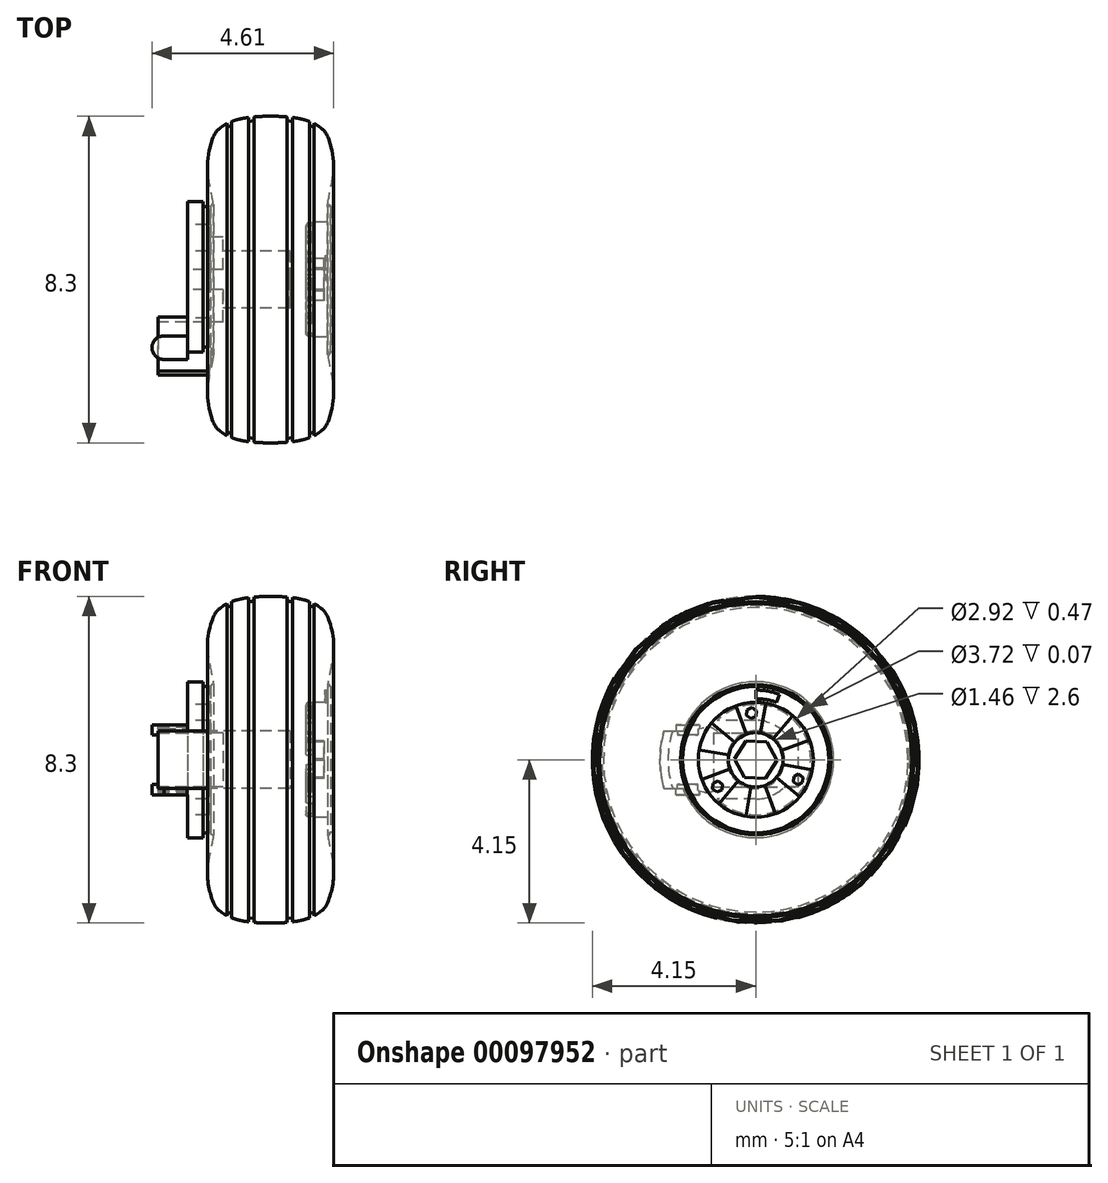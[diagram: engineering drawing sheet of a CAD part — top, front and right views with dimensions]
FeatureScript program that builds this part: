
annotation { "Feature Type Name" : "Feature", "Feature Type Description" : "" }
export const myFeature = defineFeature(function(context is Context, id is Id, definition is map)
    precondition{}
    {
        {
            var Q0;
            Q0=qCreatedBy(makeId("Front.planeOp"),FACE);
            var sketch = newSketch(context, id + "F0", { "sketchPlane" : qUnion([Q0])});
            skLineSegment(sketch, "E0.bottom", {"start": v(0, 0) * mm, "end": v(1.1, 0) * mm});
            skLineSegment(sketch, "E0.top", {"start": v(0.98, 0.7) * mm, "end": v(1.1, 0.7) * mm});
            skLineSegment(sketch, "E0.right", {"start": v(1.11, 0) * mm, "end": v(1.11, 0.7) * mm});
            skLineSegment(sketch, "E1", {"start": v(0.9, 0.77) * mm, "end": v(0.9, 1.38) * mm});
            skLineSegment(sketch, "E2", {"start": v(0.98, 1.46) * mm, "end": v(1.27, 1.46) * mm});
            skLineSegment(sketch, "E3", {"start": v(1.45, 1.64) * mm, "end": v(1.45, 1.86) * mm});
            skLineSegment(sketch, "E4", {"start": v(1.45, 1.91) * mm, "end": v(1.45, 1.91) * mm});
            skLineSegment(sketch, "E5", {"start": v(1.52, 1.91) * mm, "end": v(1.52, 1.91) * mm});
            skLineSegment(sketch, "E6", {"start": v(1.47, 1.91) * mm, "end": v(1.45, 1.91) * mm});
            skPoint(sketch, "E7.orphan", {"position": v(0, 1.46) * mm});
            skPoint(sketch, "E8.visualSharp", {"position": v(1.45, 1.46) * mm});
            skPoint(sketch, "E9.visualSharp", {"position": v(0.9, 1.46) * mm});
            skArc(sketch, "E9.filletArc", {"start": v(0.98, 1.46) * mm, "mid": v(0.92, 1.44) * mm, "end": v(0.9, 1.38) * mm});
            skArc(sketch, "E10.filletArc", {"start": v(0.9, 0.77) * mm, "mid": v(0.92, 0.71) * mm, "end": v(0.98, 0.7) * mm});
            skPoint(sketch, "E11.visualSharp", {"position": v(1.52, 1.91) * mm});
            skArc(sketch, "E11.filletArc", {"start": v(1.52, 1.86) * mm, "mid": v(1.5, 1.9) * mm, "end": v(1.47, 1.91) * mm});
            skLineSegment(sketch, "E12", {"start": v(-0.76, 4.15) * mm, "end": v(0, 4.15) * mm, "construction": true});
            skLineSegment(sketch, "E13", {"start": v(1.6, 4.08) * mm, "end": v(1.6, 0.98) * mm, "construction": true});
            skFitSpline(sketch, "E14", {"points": [v(0, 4.15) * mm, v(1.28, 3.85) * mm, v(1.4, 3.73) * mm, v(1.6, 2.99) * mm, v(1.45, 1.91) * mm], "startDerivative": vector(8.32, 0) * mm, "endDerivative": vector(-0.59, -3.7) * mm});
            skLineSegment(sketch, "E15", {"start": v(0, 4.15) * mm, "end": v(1.72, 4.15) * mm, "construction": true});
            skLineSegment(sketch, "E16", {"start": v(0.42, 4.03) * mm, "end": v(0.56, 4.02) * mm});
            skLineSegment(sketch, "E17", {"start": v(0.99, 3.92) * mm, "end": v(1.1, 3.87) * mm});
            skLineSegment(sketch, "E18", {"start": v(0.42, 4.03) * mm, "end": v(0.42, 4.13) * mm});
            skLineSegment(sketch, "E19", {"start": v(0.56, 4.02) * mm, "end": v(0.56, 4.12) * mm});
            skLineSegment(sketch, "E20", {"start": v(0.99, 3.92) * mm, "end": v(0.99, 4.02) * mm});
            skLineSegment(sketch, "E21", {"start": v(1.1, 3.87) * mm, "end": v(1.1, 3.97) * mm});
            skLineSegment(sketch, "E22", {"start": v(1.52, 1.86) * mm, "end": v(1.45, 1.86) * mm});
            skLineSegment(sketch, "E23", {"start": v(1.27, 1.46) * mm, "end": v(1.45, 1.46) * mm});
            skLineSegment(sketch, "E24", {"start": v(1.45, 1.46) * mm, "end": v(1.45, 1.64) * mm});
            skLineSegment(sketch, "E25.MirrorCS", {"start": v(-1.11, 0) * mm, "end": v(-1.11, 0.7) * mm, "construction": true});
            skLineSegment(sketch, "E26.MirrorCS", {"start": v(-0.98, 0.7) * mm, "end": v(-1.1, 0.7) * mm, "construction": true});
            skArc(sketch, "E27.MirrorCS", {"start": v(-0.9, 0.77) * mm, "mid": v(-0.92, 0.71) * mm, "end": v(-0.98, 0.7) * mm, "construction": true});
            skLineSegment(sketch, "E28.MirrorCS", {"start": v(-0.9, 0.77) * mm, "end": v(-0.9, 1.38) * mm, "construction": true});
            skArc(sketch, "E29.MirrorCS", {"start": v(-1.52, 1.86) * mm, "mid": v(-1.5, 1.9) * mm, "end": v(-1.47, 1.91) * mm});
            skLineSegment(sketch, "E30.MirrorCS", {"start": v(-1.47, 1.91) * mm, "end": v(-1.45, 1.91) * mm});
            skLineSegment(sketch, "E31", {"start": v(-2.1, 1.98) * mm, "end": v(-2.1, 1.4) * mm});
            skLineSegment(sketch, "E32", {"start": v(-2.1, 1.98) * mm, "end": v(-1.71, 1.98) * mm});
            skLineSegment(sketch, "E33", {"start": v(-2.1, 1.4) * mm, "end": v(-1.61, 1.4) * mm});
            skPoint(sketch, "E34.orphan", {"position": v(-2.1, 0.82) * mm});
            skLineSegment(sketch, "E35", {"start": v(-1.61, 0.73) * mm, "end": v(0.49, 0.73) * mm});
            skLineSegment(sketch, "E36", {"start": v(0.49, 0) * mm, "end": v(0.49, 0.96) * mm});
            skLineSegment(sketch, "E37", {"start": v(-0.97, 1.4) * mm, "end": v(-0.97, 0.96) * mm, "construction": true});
            skLineSegment(sketch, "E38", {"start": v(-1.71, 1.98) * mm, "end": v(-1.71, 1.86) * mm});
            skLineSegment(sketch, "E39", {"start": v(-1.52, 1.86) * mm, "end": v(-1.71, 1.86) * mm});
            skLineSegment(sketch, "E40", {"start": v(-2.64, 1.27) * mm, "end": v(-2.64, -0.73) * mm, "construction": true});
            skLineSegment(sketch, "E41", {"start": v(-1.61, 1.4) * mm, "end": v(-1.61, 0.73) * mm});
            skPoint(sketch, "E42.orphan", {"position": v(0, 0.73) * mm});
            skLineSegment(sketch, "E43", {"start": v(-1.61, 1.4) * mm, "end": v(-0.97, 1.4) * mm, "construction": true});
            skLineSegment(sketch, "E44", {"start": v(0, 0.73) * mm, "end": v(0, 5.2) * mm, "construction": true});
            skLineSegment(sketch, "E45.MirrorCS", {"start": v(-1.1, 3.87) * mm, "end": v(-1.1, 3.97) * mm});
            skLineSegment(sketch, "E46.MirrorCS", {"start": v(-0.99, 3.92) * mm, "end": v(-1.1, 3.87) * mm});
            skLineSegment(sketch, "E47.MirrorCS", {"start": v(-0.99, 3.92) * mm, "end": v(-0.99, 4.02) * mm});
            skFitSpline(sketch, "E48.MirrorCS", {"points": [v(0, 4.15) * mm, v(-1.28, 3.85) * mm, v(-1.4, 3.73) * mm, v(-1.6, 2.99) * mm, v(-1.45, 1.91) * mm], "startDerivative": vector(-8.32, 0) * mm, "endDerivative": vector(0.59, -3.7) * mm});
            skLineSegment(sketch, "E49.MirrorCS", {"start": v(-0.42, 4.03) * mm, "end": v(-0.56, 4.02) * mm});
            skLineSegment(sketch, "E50.MirrorCS", {"start": v(-0.42, 4.03) * mm, "end": v(-0.42, 4.13) * mm});
            skLineSegment(sketch, "E51.MirrorCS", {"start": v(-0.56, 4.02) * mm, "end": v(-0.56, 4.12) * mm});
            skLineSegment(sketch, "E52.MirrorCS", {"start": v(-1.52, 1.91) * mm, "end": v(-1.52, 1.91) * mm});
            skFitSpline(sketch, "E53.MirrorCS", {"points": [v(0, 4.15) * mm, v(-1.28, 3.85) * mm, v(-1.4, 3.73) * mm, v(-1.6, 2.99) * mm, v(-1.45, 1.91) * mm], "startDerivative": vector(-8.32, 0) * mm, "endDerivative": vector(0.59, -3.7) * mm});
            skSolve(sketch);
        }
        {
            var Q0;
            Q0=makeQuery(id+"F0.imprint","IMPRINT",FACE,{"disambiguationData":[TD([[makeQuery(id+"F0.imprint","IMPRINT",EDGE,{"derivedFrom":sQuery(id+"F0.wireOp",EDGE,"E0.top")}),-1.0]])]});
            var Q1;
            Q1=sQuery(id+"F0.wireOp",EDGE,"E25.MirrorCS");
            var Q2;
            Q2=sQuery(id+"F0.wireOp",EDGE,"E28.MirrorCS");
            var Q3;
            Q3=sQuery(id+"F0.wireOp",EDGE,"E27.MirrorCS");
            var Q4;
            Q4=sQuery(id+"F0.wireOp",EDGE,"E26.MirrorCS");
            var Q5;
            Q5=sQuery(id+"F0.wireOp",EDGE,"E0.bottom");
            revolve(context, id + "F1", {"entities" : qUnion([Q0]), "surfaceEntities" : qUnion([Q1, Q2, Q3, Q4]), "axis" : qUnion([Q5]), "revolveType" : RevolveType.FULL});
        }
        {
            var Q0;
            Q0=makeQuery(id+"F1.opRevolve","SWEPT_FACE",FACE,{"disambiguationData":[OSD([sQuery(id+"F0.wireOp",EDGE,"E31")])]});
            var sketch = newSketch(context, id + "F2", { "sketchPlane" : qUnion([Q0])});
            skArc(sketch, "E54", {"start": v(0, 1) * mm, "mid": v(-1, 0) * mm, "end": v(0, -1) * mm});
            skLineSegment(sketch, "E55", {"start": v(0, 1) * mm, "end": v(0.98, 1) * mm});
            skLineSegment(sketch, "E56", {"start": v(0, -1) * mm, "end": v(0.98, -1) * mm});
            skArc(sketch, "E57", {"start": v(0.98, -1) * mm, "mid": v(1.4, 0) * mm, "end": v(0.98, 1) * mm});
            skCircle(sketch, "E58", {"center": v(0, 0) * mm, "radius": 0.73 * mm});
            skSolve(sketch);
        }
        {
            var Q0;
            Q0 = qSketchRegion(id + "F2", true);
            var Q1;
            Q1=makeQuery(id+"F1.opRevolve","SWEPT_FACE",FACE,{"disambiguationData":[OSD([sQuery(id+"F0.wireOp",EDGE,"E41")])]});
            extrude(context, id + "F3", {"entities" : qUnion([Q0]), "operationType" : NewBodyOperationType.ADD, "endBound" : BoundingType.UP_TO_SURFACE, "oppositeDirection" : true, "endBoundEntityFace" : qUnion([Q1]), "depth" : 25 * mm});
        }
        {
            var Q0;
            Q0=makeQuery(id+"F3.boolean.opBoolean","MERGE",FACE,{"derivedFrom":[makeQuery(id+"F1.opRevolve","SWEPT_FACE",FACE,{"disambiguationData":[OSD([sQuery(id+"F0.wireOp",EDGE,"E31")])]}),makeQuery(id+"F3.opExtrude","CAP_FACE",FACE,{"disambiguationData":[OSD([sQuery(id+"F2.wireOp",EDGE,"E54"),sQuery(id+"F2.wireOp",EDGE,"E55"),sQuery(id+"F2.wireOp",EDGE,"E56"),sQuery(id+"F2.wireOp",EDGE,"E58"),sQuery(id+"F2.wireOp",EDGE,"E57")])],"isStart":true})]});
            var sketch = newSketch(context, id + "F4", { "sketchPlane" : qUnion([Q0])});
            skLineSegment(sketch, "E59.bottom", {"start": v(1.08, 0.68) * mm, "end": v(-1.08, 0.69) * mm});
            skLineSegment(sketch, "E59.top", {"start": v(1.08, -0.69) * mm, "end": v(-1.08, -0.68) * mm});
            skLineSegment(sketch, "E59.left", {"start": v(1.08, 0.68) * mm, "end": v(1.08, -0.69) * mm});
            skLineSegment(sketch, "E59.right", {"start": v(-1.08, 0.69) * mm, "end": v(-1.08, -0.68) * mm});
            skPoint(sketch, "E59.middle", {"position": v(0, 0) * mm});
            skSolve(sketch);
        }
        {
            var Q0;
            Q0 = qSketchRegion(id + "F4", true);
            extrude(context, id + "F5", {"entities" : qUnion([Q0]), "operationType" : NewBodyOperationType.REMOVE, "oppositeDirection" : true, "depth" : 0.9 * mm});
        }
        {
            var Q0;
            Q0=makeQuery(id+"F3.boolean.opBoolean","MERGE",FACE,{"derivedFrom":[makeQuery(id+"F1.opRevolve","SWEPT_FACE",FACE,{"disambiguationData":[OSD([sQuery(id+"F0.wireOp",EDGE,"E31")])]}),makeQuery(id+"F3.opExtrude","CAP_FACE",FACE,{"disambiguationData":[OSD([sQuery(id+"F2.wireOp",EDGE,"E54"),sQuery(id+"F2.wireOp",EDGE,"E55"),sQuery(id+"F2.wireOp",EDGE,"E56"),sQuery(id+"F2.wireOp",EDGE,"E58"),sQuery(id+"F2.wireOp",EDGE,"E57")])],"isStart":true})]});
            var sketch = newSketch(context, id + "F6", { "sketchPlane" : qUnion([Q0])});
            skLineSegment(sketch, "E60", {"start": v(2.33, 0.73) * mm, "end": v(2.33, -0.73) * mm, "construction": true});
            skLineSegment(sketch, "E61", {"start": v(0, 0) * mm, "end": v(2.43, 0) * mm, "construction": true});
            skArc(sketch, "E62", {"start": v(2.43, 0) * mm, "mid": v(2.4, 0.37) * mm, "end": v(2.33, 0.73) * mm});
            skLineSegment(sketch, "E63", {"start": v(2.33, 0.73) * mm, "end": v(1.68, 0.73) * mm});
            skLineSegment(sketch, "E64", {"start": v(2.65, 0.83) * mm, "end": v(-0.85, 0.83) * mm, "construction": true});
            skLineSegment(sketch, "E65", {"start": v(0.89, 2.3) * mm, "end": v(0.9, -2.15) * mm, "construction": true});
            skLineSegment(sketch, "E66", {"start": v(1.23, 1.18) * mm, "end": v(1.23, 0.25) * mm, "construction": true});
            skLineSegment(sketch, "E67", {"start": v(1.57, 0.49) * mm, "end": v(0.7, 0.49) * mm, "construction": true});
            skArc(sketch, "E68", {"start": v(1.31, 0.82) * mm, "mid": v(1.11, 0.8) * mm, "end": v(0.95, 0.68) * mm});
            skLineSegment(sketch, "E69", {"start": v(1.68, 0.73) * mm, "end": v(1.27, 0.83) * mm});
            skLineSegment(sketch, "E70", {"start": v(0.95, 0.68) * mm, "end": v(1.08, 0.68) * mm});
            skLineSegment(sketch, "E71", {"start": v(1.08, 0.68) * mm, "end": v(1.08, 0) * mm});
            skLineSegment(sketch, "E72", {"start": v(1.08, 0) * mm, "end": v(2.43, 0) * mm});
            skArc(sketch, "E73.MirrorCS", {"start": v(2.43, 0) * mm, "mid": v(2.4, -0.37) * mm, "end": v(2.33, -0.73) * mm});
            skLineSegment(sketch, "E74.MirrorCS", {"start": v(2.33, -0.73) * mm, "end": v(1.68, -0.73) * mm});
            skLineSegment(sketch, "E75.MirrorCS", {"start": v(1.68, -0.73) * mm, "end": v(1.27, -0.83) * mm});
            skArc(sketch, "E76.MirrorCS", {"start": v(1.31, -0.82) * mm, "mid": v(1.11, -0.8) * mm, "end": v(0.95, -0.68) * mm});
            skLineSegment(sketch, "E77.MirrorCS", {"start": v(0.95, -0.68) * mm, "end": v(1.08, -0.68) * mm});
            skLineSegment(sketch, "E78.MirrorCS", {"start": v(1.08, -0.68) * mm, "end": v(1.08, 0) * mm});
            skSolve(sketch);
        }
        {
            var Q0;
            Q0 = qSketchRegion(id + "F6", true);
            extrude(context, id + "F7", {"entities" : qUnion([Q0]), "operationType" : NewBodyOperationType.ADD, "depth" : 0.75 * mm, "hasSecondDirection" : true, "secondDirectionOppositeDirection" : true, "secondDirectionDepth" : 0.6 * mm});
        }
        {
            var Q0;
            Q0=makeQuery(id+"F7.opExtrude","SWEPT_FACE",FACE,{"disambiguationData":[OSD([sQuery(id+"F6.wireOp",EDGE,"E63")])]});
            var sketch = newSketch(context, id + "F8", { "sketchPlane" : qUnion([Q0])});
            skLineSegment(sketch, "E79", {"start": v(-2.7, -1.43) * mm, "end": v(-2.7, -2.03) * mm, "construction": true});
            skArc(sketch, "E80", {"start": v(-2.7, -1.43) * mm, "mid": v(-3, -1.73) * mm, "end": v(-2.7, -2.03) * mm});
            skLineSegment(sketch, "E81", {"start": v(-2.1, -2.03) * mm, "end": v(-2.1, -1.43) * mm});
            skLineSegment(sketch, "E82", {"start": v(-2.7, -1.43) * mm, "end": v(-2.1, -1.43) * mm});
            skLineSegment(sketch, "E83", {"start": v(-2.7, -2.03) * mm, "end": v(-2.1, -2.03) * mm});
            skSolve(sketch);
        }
        {
            var Q0;
            Q0 = qSketchRegion(id + "F8", true);
            extrude(context, id + "F9", {"entities" : qUnion([Q0]), "operationType" : NewBodyOperationType.ADD, "depth" : 0.16 * mm, "hasSecondDirection" : true, "secondDirectionOppositeDirection" : true, "secondDirectionDepth" : 0.1 * mm});
        }
        {
            var Q0;
            Q0=makeQuery(id+"F7.opExtrude","SWEPT_FACE",FACE,{"disambiguationData":[OSD([sQuery(id+"F6.wireOp",EDGE,"E74.MirrorCS")])]});
            var sketch = newSketch(context, id + "F10", { "sketchPlane" : qUnion([Q0])});
            skArc(sketch, "E84", {"start": v(-2.7, 2.03) * mm, "mid": v(-3.01, 1.73) * mm, "end": v(-2.7, 1.43) * mm});
            skLineSegment(sketch, "E85", {"start": v(-2.7, 1.43) * mm, "end": v(-2.12, 1.43) * mm});
            skLineSegment(sketch, "E86", {"start": v(-2.12, 1.43) * mm, "end": v(-2.12, 2.03) * mm});
            skLineSegment(sketch, "E87", {"start": v(-2.72, 2.03) * mm, "end": v(-2.12, 2.03) * mm});
            skSolve(sketch);
        }
        {
            var Q0;
            Q0 = qSketchRegion(id + "F10", true);
            extrude(context, id + "F11", {"entities" : qUnion([Q0]), "operationType" : NewBodyOperationType.ADD, "depth" : 0.16 * mm, "hasSecondDirection" : true, "secondDirectionOppositeDirection" : true, "secondDirectionDepth" : 0.1 * mm});
        }
        {
            var Q0;
            Q0=makeQuery(id+"F1.opRevolve","SWEPT_FACE",FACE,{"disambiguationData":[OSD([sQuery(id+"F0.wireOp",EDGE,"E0.right")])]});
            var sketch = newSketch(context, id + "F12", { "sketchPlane" : qUnion([Q0])});
            skCircle(sketch, "E88.cCircle", {"center": v(0, 0) * mm, "radius": 0.47 * mm, "construction": true});
            skLineSegment(sketch, "E88.0", {"start": v(0.29, 0.45) * mm, "end": v(0.54, -0.02) * mm});
            skLineSegment(sketch, "E88.1", {"start": v(0.54, -0.02) * mm, "end": v(0.25, -0.48) * mm});
            skLineSegment(sketch, "E88.2", {"start": v(0.25, -0.48) * mm, "end": v(-0.29, -0.45) * mm});
            skLineSegment(sketch, "E88.3", {"start": v(-0.29, -0.45) * mm, "end": v(-0.54, 0.02) * mm});
            skLineSegment(sketch, "E88.4", {"start": v(-0.54, 0.02) * mm, "end": v(-0.25, 0.48) * mm});
            skLineSegment(sketch, "E88.5", {"start": v(-0.25, 0.48) * mm, "end": v(0.29, 0.45) * mm});
            skPoint(sketch, "E88.0.midPoint", {"position": v(0.41, 0.22) * mm});
            skSolve(sketch);
        }
        {
            var Q0;
            Q0 = qSketchRegion(id + "F12", true);
            extrude(context, id + "F13", {"entities" : qUnion([Q0]), "operationType" : NewBodyOperationType.ADD, "depth" : 0.25 * mm});
        }
        {
            var Q0;
            Q0=makeQuery(id+"F1.opRevolve","SWEPT_FACE",FACE,{"disambiguationData":[OSD([sQuery(id+"F0.wireOp",EDGE,"E1")])]});
            var sketch = newSketch(context, id + "F14", { "sketchPlane" : qUnion([Q0])});
            skPoint(sketch, "E89.center", {"position": v(0, 0) * mm});
            skCircle(sketch, "E90.cCircle", {"center": v(-0.1, 1.19) * mm, "radius": 0.12 * mm, "construction": true});
            skLineSegment(sketch, "E90.0", {"start": v(-0.23, 1.13) * mm, "end": v(-0.22, 1.26) * mm});
            skLineSegment(sketch, "E90.1", {"start": v(-0.22, 1.26) * mm, "end": v(-0.1, 1.32) * mm});
            skLineSegment(sketch, "E90.2", {"start": v(-0.1, 1.32) * mm, "end": v(0.02, 1.24) * mm});
            skLineSegment(sketch, "E90.3", {"start": v(0.02, 1.24) * mm, "end": v(0, 1.1) * mm});
            skLineSegment(sketch, "E90.4", {"start": v(0, 1.1) * mm, "end": v(-0.12, 1.05) * mm});
            skLineSegment(sketch, "E90.5", {"start": v(-0.12, 1.05) * mm, "end": v(-0.23, 1.13) * mm});
            skPoint(sketch, "E90.0.midPoint", {"position": v(-0.22, 1.2) * mm});
            skLineSegment(sketch, "E91", {"start": v(0, 0) * mm, "end": v(-0.1, 1.19) * mm, "construction": true});
            skLineSegment(sketch, "E92.1.0", {"start": v(-0.86, -0.76) * mm, "end": v(-0.99, -0.82) * mm});
            skLineSegment(sketch, "E92.1.1", {"start": v(-0.99, -0.82) * mm, "end": v(-1.1, -0.74) * mm});
            skLineSegment(sketch, "E92.1.2", {"start": v(-1.1, -0.74) * mm, "end": v(-1.09, -0.6) * mm});
            skLineSegment(sketch, "E92.1.3", {"start": v(-1.09, -0.6) * mm, "end": v(-0.96, -0.54) * mm});
            skLineSegment(sketch, "E92.1.4", {"start": v(-0.96, -0.54) * mm, "end": v(-0.85, -0.62) * mm});
            skLineSegment(sketch, "E92.1.5", {"start": v(-0.85, -0.62) * mm, "end": v(-0.86, -0.76) * mm});
            skCircle(sketch, "E92.1.6", {"center": v(-0.97, -0.68) * mm, "radius": 0.12 * mm, "construction": true});
            skLineSegment(sketch, "E92.2.0", {"start": v(1.1, -0.36) * mm, "end": v(1.2, -0.44) * mm});
            skLineSegment(sketch, "E92.2.1", {"start": v(1.2, -0.44) * mm, "end": v(1.2, -0.58) * mm});
            skLineSegment(sketch, "E92.2.2", {"start": v(1.2, -0.58) * mm, "end": v(1.07, -0.64) * mm});
            skLineSegment(sketch, "E92.2.3", {"start": v(1.07, -0.64) * mm, "end": v(0.95, -0.56) * mm});
            skLineSegment(sketch, "E92.2.4", {"start": v(0.95, -0.56) * mm, "end": v(0.96, -0.42) * mm});
            skLineSegment(sketch, "E92.2.5", {"start": v(0.96, -0.42) * mm, "end": v(1.1, -0.36) * mm});
            skCircle(sketch, "E92.2.6", {"center": v(1.08, -0.5) * mm, "radius": 0.12 * mm, "construction": true});
            skSolve(sketch);
        }
        {
            var Q0;
            Q0 = qSketchRegion(id + "F14", true);
            extrude(context, id + "F15", {"entities" : qUnion([Q0]), "operationType" : NewBodyOperationType.ADD, "depth" : 0.15 * mm});
        }
        {
            var Q0;
            Q0=qCreatedBy(makeId("Front.planeOp"),FACE);
            var sketch = newSketch(context, id + "F16", { "sketchPlane" : qUnion([Q0])});
            skLineSegment(sketch, "E93.bottom", {"start": v(1.39, 1.77) * mm, "end": v(1.6, 1.77) * mm});
            skLineSegment(sketch, "E93.top", {"start": v(1.4, 1.55) * mm, "end": v(1.6, 1.55) * mm});
            skLineSegment(sketch, "E93.left", {"start": v(1.4, 1.77) * mm, "end": v(1.4, 1.55) * mm});
            skLineSegment(sketch, "E93.right", {"start": v(1.6, 1.77) * mm, "end": v(1.6, 1.55) * mm});
            skLineSegment(sketch, "E94", {"start": v(0, 0) * mm, "end": v(2.72, 0) * mm, "construction": true});
            skSolve(sketch);
        }
        {
            var Q0;
            Q0 = qSketchRegion(id + "F16", true);
            var Q1;
            Q1=sQuery(id+"F16.wireOp",EDGE,"E94");
            revolve(context, id + "F17", {"operationType" : NewBodyOperationType.REMOVE, "entities" : qUnion([Q0]), "axis" : qUnion([Q1]), "revolveType" : RevolveType.ONE_DIRECTION, "oppositeDirection" : true, "angle" : 20 * degree});
        }
        {
            var Q0;
            Q0=makeQuery(id+"F1.opRevolve","SWEPT_FACE",FACE,{"disambiguationData":[OSD([sQuery(id+"F0.wireOp",EDGE,"E1")])]});
            var sketch = newSketch(context, id + "F18", { "sketchPlane" : qUnion([Q0])});
            skLineSegment(sketch, "E95", {"start": v(0.1, 0.62) * mm, "end": v(0.26, 1.48) * mm});
            skLineSegment(sketch, "E96", {"start": v(0.4, 0.48) * mm, "end": v(0.96, 1.15) * mm});
            skArc(sketch, "E97", {"start": v(0.26, 1.48) * mm, "mid": v(0.63, 1.36) * mm, "end": v(0.96, 1.15) * mm});
            skArc(sketch, "E98", {"start": v(0.1, 0.62) * mm, "mid": v(0.27, 0.57) * mm, "end": v(0.4, 0.48) * mm});
            skLineSegment(sketch, "E99.1.0", {"start": v(-0.48, 0.4) * mm, "end": v(-1.15, 0.96) * mm});
            skArc(sketch, "E99.1.1", {"start": v(-1.15, 0.96) * mm, "mid": v(-0.86, 1.23) * mm, "end": v(-0.51, 1.4) * mm});
            skLineSegment(sketch, "E99.1.2", {"start": v(-0.22, 0.6) * mm, "end": v(-0.51, 1.4) * mm});
            skArc(sketch, "E99.1.3", {"start": v(-0.48, 0.4) * mm, "mid": v(-0.36, 0.52) * mm, "end": v(-0.22, 0.6) * mm});
            skLineSegment(sketch, "E99.anchor1", {"start": v(0, 0) * mm, "end": v(0, 0) * mm});
            skLineSegment(sketch, "E99.anchor2", {"start": v(0, 0) * mm, "end": v(0, 0) * mm});
            skArc(sketch, "E100.3.2.0", {"start": v(-1.4, -0.51) * mm, "mid": v(-1.5, -0.13) * mm, "end": v(-1.48, 0.26) * mm});
            skLineSegment(sketch, "E100.4.2.0", {"start": v(-0.6, -0.22) * mm, "end": v(-1.4, -0.51) * mm});
            skLineSegment(sketch, "E100.7.2.0", {"start": v(-0.62, 0.1) * mm, "end": v(-1.48, 0.26) * mm});
            skArc(sketch, "E100.10.2.0", {"start": v(-0.6, -0.22) * mm, "mid": v(-0.63, -0.05) * mm, "end": v(-0.62, 0.1) * mm});
            skArc(sketch, "E100.3.3.0", {"start": v(-0.26, -1.48) * mm, "mid": v(-0.63, -1.36) * mm, "end": v(-0.96, -1.15) * mm});
            skLineSegment(sketch, "E100.4.3.0", {"start": v(-0.1, -0.62) * mm, "end": v(-0.26, -1.48) * mm});
            skLineSegment(sketch, "E100.7.3.0", {"start": v(-0.4, -0.48) * mm, "end": v(-0.96, -1.15) * mm});
            skArc(sketch, "E100.10.3.0", {"start": v(-0.1, -0.62) * mm, "mid": v(-0.27, -0.57) * mm, "end": v(-0.4, -0.48) * mm});
            skArc(sketch, "E100.3.4.0", {"start": v(1.15, -0.96) * mm, "mid": v(0.86, -1.23) * mm, "end": v(0.51, -1.4) * mm});
            skLineSegment(sketch, "E100.4.4.0", {"start": v(0.48, -0.4) * mm, "end": v(1.15, -0.96) * mm});
            skLineSegment(sketch, "E100.7.4.0", {"start": v(0.22, -0.6) * mm, "end": v(0.51, -1.4) * mm});
            skArc(sketch, "E100.10.4.0", {"start": v(0.48, -0.4) * mm, "mid": v(0.36, -0.52) * mm, "end": v(0.22, -0.6) * mm});
            skArc(sketch, "E100.3.5.0", {"start": v(1.4, 0.51) * mm, "mid": v(1.5, 0.13) * mm, "end": v(1.48, -0.26) * mm});
            skLineSegment(sketch, "E100.4.5.0", {"start": v(0.6, 0.22) * mm, "end": v(1.4, 0.51) * mm});
            skLineSegment(sketch, "E100.7.5.0", {"start": v(0.62, -0.1) * mm, "end": v(1.48, -0.26) * mm});
            skArc(sketch, "E100.10.5.0", {"start": v(0.6, 0.22) * mm, "mid": v(0.63, 0.05) * mm, "end": v(0.62, -0.1) * mm});
            skSolve(sketch);
        }
        {
            var Q0;
            Q0 = qSketchRegion(id + "F18", true);
            extrude(context, id + "F19", {"entities" : qUnion([Q0]), "operationType" : NewBodyOperationType.ADD, "depth" : .18 * mm});
        }
    });
